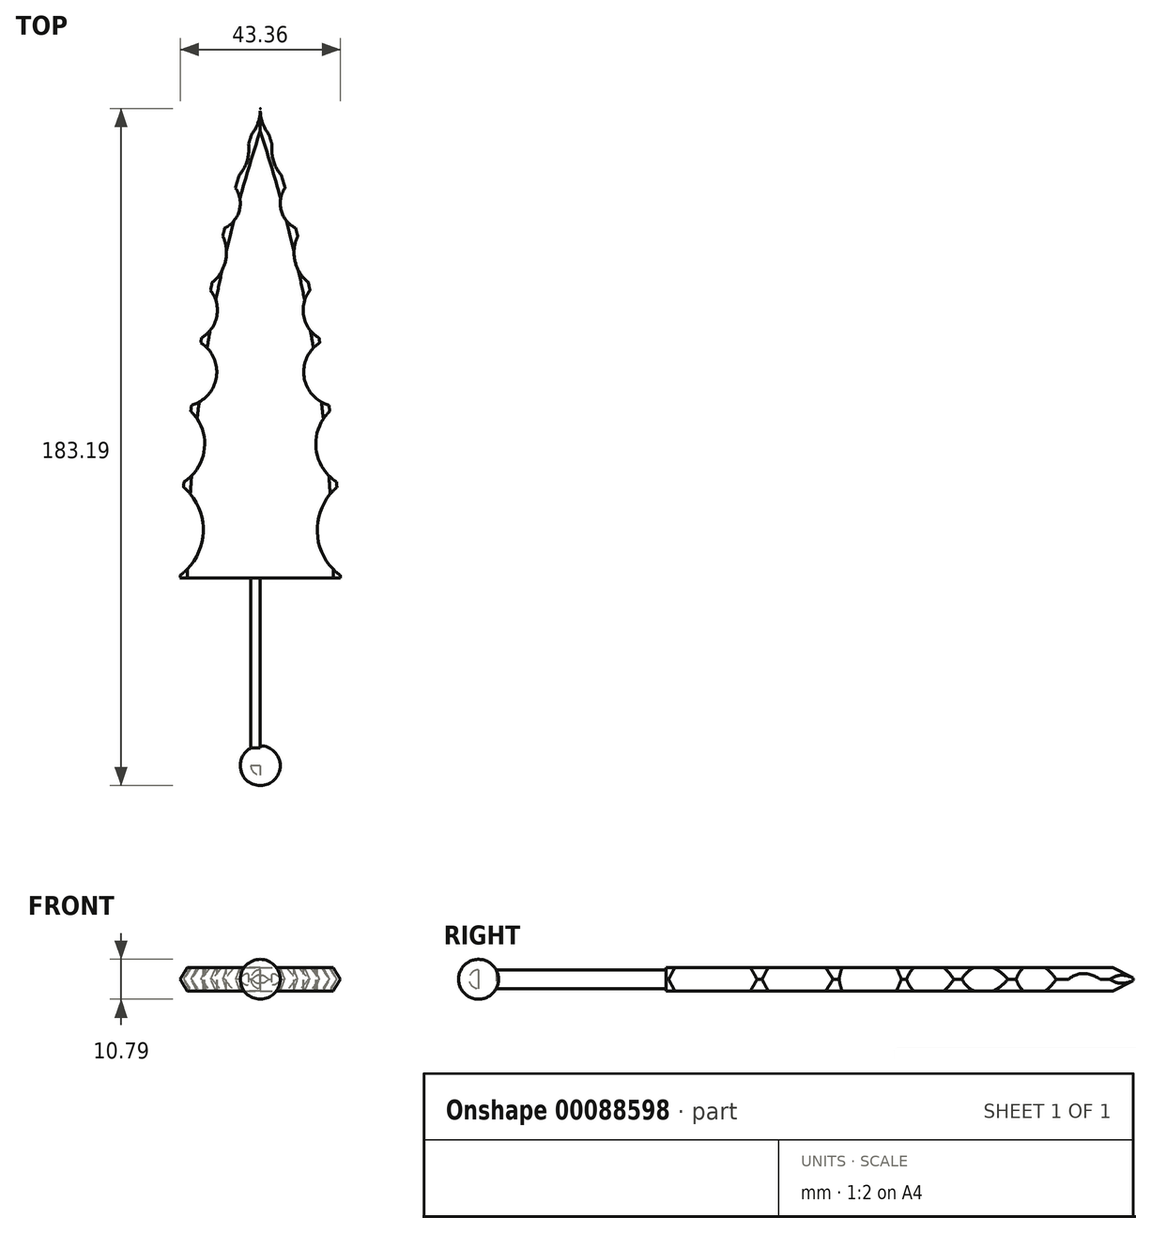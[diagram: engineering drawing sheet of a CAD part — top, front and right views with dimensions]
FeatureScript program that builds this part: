
annotation { "Feature Type Name" : "Feature", "Feature Type Description" : "" }
export const myFeature = defineFeature(function(context is Context, id is Id, definition is map)
    precondition{}
    {
        {
            var Q0;
            Q0=qCreatedBy(makeId("Top.planeOp"),FACE);
            var sketch = newSketch(context, id + "F0", { "sketchPlane" : qUnion([Q0])});
            skLineSegment(sketch, "E0", {"start": v(0, 0) * mm, "end": v(0, -127) * mm});
            skArc(sketch, "E1", {"start": v(0, 0) * mm, "mid": v(-15.98, -62.62) * mm, "end": v(-21.68, -127) * mm});
            skLineSegment(sketch, "E2", {"start": v(-21.68, -127) * mm, "end": v(0, -127) * mm});
            skSolve(sketch);
        }
        {
            var Q0;
            Q0=makeQuery(id+"F0.imprint","IMPRINT",FACE,{"disambiguationData":[TD([[makeQuery(id+"F0.imprint","IMPRINT",EDGE,{"derivedFrom":sQuery(id+"F0.wireOp",EDGE,"E0")}),-1.0]])]});
            extrude(context, id + "F1", {"entities" : qUnion([Q0]), "depth" : 6.35 * mm});
        }
        {
            var Q0;
            Q0=makeQuery(id+"F1.opExtrude","SWEPT_FACE",FACE,{"disambiguationData":[OSD([sQuery(id+"F0.wireOp",EDGE,"E0")])]});
            var sketch = newSketch(context, id + "F2", { "sketchPlane" : qUnion([Q0])});
            skLineSegment(sketch, "E3", {"start": v(0, 3.17) * mm, "end": v(-6.1, 6.35) * mm});
            skLineSegment(sketch, "E4", {"start": v(0, 3.18) * mm, "end": v(-6.1, 0) * mm});
            skLineSegment(sketch, "E5", {"start": v(-6.1, 6.35) * mm, "end": v(0, 6.35) * mm});
            skLineSegment(sketch, "E6", {"start": v(0, 6.35) * mm, "end": v(0, 0) * mm});
            skLineSegment(sketch, "E7", {"start": v(0, 0) * mm, "end": v(-6.1, 0) * mm});
            skSolve(sketch);
        }
        {
            var Q0;
            {var subQ0=sQuery(id+"F2.wireOp",EDGE,"E3");Q0=makeQuery(id+"F2.imprint","IMPRINT",FACE,{"disambiguationData":[TD([[makeQuery(id+"F2.imprint","IMPRINT",EDGE,{"derivedFrom":subQ0}),-1.0]])]});}
            var Q1;
            {var subQ0=sQuery(id+"F2.wireOp",EDGE,"E4");Q1=makeQuery(id+"F2.imprint","IMPRINT",FACE,{"disambiguationData":[TD([[makeQuery(id+"F2.imprint","IMPRINT",EDGE,{"derivedFrom":subQ0}),1.0]])]});}
            var Q2;
            Q2=makeQuery(id+"F1.opExtrude","CAP_EDGE",EDGE,{"disambiguationData":[OSD([sQuery(id+"F0.wireOp",EDGE,"E1")])],"isStart":false});
            sweep(context, id + "F3", {"operationType" : NewBodyOperationType.REMOVE, "profiles" : qUnion([Q0, Q1]), "path" : qUnion([Q2])});
        }
        {
            var Q0;
            Q0=makeQuery(id+"F1.opExtrude","CAP_FACE",FACE,{"disambiguationData":[OSD([sQuery(id+"F0.wireOp",EDGE,"E0"),sQuery(id+"F0.wireOp",EDGE,"E1"),sQuery(id+"F0.wireOp",EDGE,"E2")])],"isStart":false});
            var sketch = newSketch(context, id + "F4", { "sketchPlane" : qUnion([Q0])});
            skArc(sketch, "E8", {"start": v(-22.72, -127) * mm, "mid": v(-15.43, -114.58) * mm, "end": v(-21.75, -101.65) * mm});
            skPoint(sketch, "E8.startSnap0", {"position": v(-9.87, -127) * mm});
            skArc(sketch, "E9", {"start": v(-21.75, -101.65) * mm, "mid": v(-15.06, -91.49) * mm, "end": v(-20.44, -80.57) * mm});
            skArc(sketch, "E10", {"start": v(-20.44, -80.57) * mm, "mid": v(-11.9, -72.83) * mm, "end": v(-17.4, -62.7) * mm});
            skArc(sketch, "E11", {"start": v(-17.4, -62.7) * mm, "mid": v(-11.75, -56.2) * mm, "end": v(-14.55, -48.07) * mm});
            skPoint(sketch, "E11.endSnap0", {"position": v(-14.55, -65.78) * mm});
            skArc(sketch, "E12", {"start": v(-14.55, -48.07) * mm, "mid": v(-9.4, -41.24) * mm, "end": v(-11.12, -32.87) * mm});
            skArc(sketch, "E13", {"start": v(-11.12, -32.87) * mm, "mid": v(-5.63, -27.43) * mm, "end": v(-7.98, -20.08) * mm});
            skLineSegment(sketch, "E14", {"start": v(-22.72, -127) * mm, "end": v(-51.18, -45.67) * mm});
            skArc(sketch, "E15", {"start": v(-7.98, -20.08) * mm, "mid": v(-3.8, -14.83) * mm, "end": v(-3.43, -8.13) * mm});
            skArc(sketch, "E16", {"start": v(-3.43, -8.13) * mm, "mid": v(-0.15, -2.18) * mm, "end": v(-1.22, 4.54) * mm});
            skLineSegment(sketch, "E17", {"start": v(-1.22, 4.54) * mm, "end": v(-1.22, 22.29) * mm});
            skLineSegment(sketch, "E18", {"start": v(-51.18, -45.67) * mm, "end": v(-1.22, 22.29) * mm});
            skSolve(sketch);
        }
        {
            var Q0;
            Q0 = qSketchRegion(id + "F4", true);
            extrude(context, id + "F5", {"entities" : qUnion([Q0]), "operationType" : NewBodyOperationType.REMOVE, "oppositeDirection" : true, "depth" : 25.4 * mm});
        }
        {
            var Q0;
            Q0=makeQuery(id+"F5.boolean.opBoolean","SPLIT",BODY,{"disambiguationData":[OD(1.0)],"derivedFrom":makeQuery(id+"F1.opExtrude","SWEPT_BODY",BODY,{"disambiguationData":[OSD([sQuery(id+"F0.wireOp",EDGE,"E0"),sQuery(id+"F0.wireOp",EDGE,"E1"),sQuery(id+"F0.wireOp",EDGE,"E2")])]})});
            var Q1;
            {var subQ0=sQuery(id+"F0.wireOp",EDGE,"E1");var subQ1=sQuery(id+"F0.wireOp",EDGE,"E2");var subQ2=sQuery(id+"F0.wireOp",EDGE,"E0");Q1=makeQuery(id+"F5.boolean.opBoolean","SPLIT",FACE,{"disambiguationData":[TD([makeQuery(id+"F1.opExtrude","CAP_FACE",FACE,{"disambiguationData":[OSD([subQ2,subQ0,subQ1])],"isStart":true}),makeQuery(id+"F1.opExtrude","CAP_FACE",FACE,{"disambiguationData":[OSD([subQ2,subQ0,subQ1])],"isStart":false}),makeQuery(id+"F1.opExtrude","SWEPT_FACE",FACE,{"disambiguationData":[OSD([subQ1])]}),makeQuery(id+"F3.boolean.opBoolean","COPY",FACE,{"derivedFrom":makeQuery(id+"F3.opSweep","SWEPT_FACE",FACE,{"disambiguationData":[OSD([subQ0,sQuery(id+"F2.wireOp",EDGE,"E3")])]})}),makeQuery(id+"F3.boolean.opBoolean","COPY",FACE,{"derivedFrom":makeQuery(id+"F3.opSweep","SWEPT_FACE",FACE,{"disambiguationData":[OSD([subQ0,sQuery(id+"F2.wireOp",EDGE,"E4")])]})}),makeQuery(id+"F5.opExtrude","SWEPT_FACE",FACE,{"disambiguationData":[OSD([sQuery(id+"F4.wireOp",EDGE,"E16")])]})])],"derivedFrom":makeQuery(id+"F1.opExtrude","SWEPT_FACE",FACE,{"disambiguationData":[OSD([subQ2])]})});}
            mirror(context, id + "F6", {"operationType" : NewBodyOperationType.ADD, "entities" : qUnion([Q0]), "mirrorPlane" : qUnion([Q1])});
        }
        {
            var Q0;
            {var subQ0=makeQuery(id+"F1.opExtrude","SWEPT_FACE",FACE,{"disambiguationData":[OSD([sQuery(id+"F0.wireOp",EDGE,"E2")])]});Q0=makeQuery(id+"F6.boolean.opBoolean","MERGE",FACE,{"derivedFrom":[subQ0,makeQuery(id+"F6.opPattern","COPY",FACE,{"derivedFrom":subQ0,"instanceName":"1"})]});}
            var sketch = newSketch(context, id + "F7", { "sketchPlane" : qUnion([Q0])});
            skLineSegment(sketch, "E19.bottom", {"start": v(-19.75, 6.35) * mm, "end": v(19.75, 6.35) * mm});
            skLineSegment(sketch, "E19.top", {"start": v(-19.75, 0) * mm, "end": v(19.75, 0) * mm});
            skLineSegment(sketch, "E19.left", {"start": v(-19.75, 6.35) * mm, "end": v(-19.75, 0) * mm});
            skLineSegment(sketch, "E19.right", {"start": v(19.75, 6.35) * mm, "end": v(19.75, 0) * mm});
            skLineSegment(sketch, "E20", {"start": v(-19.75, 6.35) * mm, "end": v(-6.58, 6.35) * mm});
            skLineSegment(sketch, "E21", {"start": v(19.75, 6.35) * mm, "end": v(6.58, 6.35) * mm});
            skLineSegment(sketch, "E22", {"start": v(-6.58, 6.35) * mm, "end": v(6.58, 6.35) * mm});
            skLineSegment(sketch, "E23", {"start": v(-6.58, 6.35) * mm, "end": v(-6.58, 0) * mm});
            skLineSegment(sketch, "E24", {"start": v(6.58, 6.35) * mm, "end": v(6.58, 0) * mm});
            skLineSegment(sketch, "E25", {"start": v(-6.58, 3.18) * mm, "end": v(6.58, 3.18) * mm});
            skCircle(sketch, "E26", {"center": v(0, 3.18) * mm, "radius": 2.54 * mm});
            skSolve(sketch);
        }
        {
            var Q0;
            {var subQ0=sQuery(id+"F7.wireOp",EDGE,"TZ6vj6Sh-qNe0-tSPx-zquS-x5aDAgaGdUHA");var subQ1=sQuery(id+"F7.wireOp",EDGE,"E25");var subQ2=makeQuery(id+"F7.imprint","INTERSECT",VERTEX,{"disambiguationData":[OD(0.0)],"derivedFrom":[subQ1,subQ0]});Q0=makeQuery(id+"F7.imprint","IMPRINT",FACE,{"disambiguationData":[TD([[makeQuery(id+"F7.imprint","IMPRINT",EDGE,{"disambiguationData":[TD([[subQ2,-1.0]])],"derivedFrom":subQ1}),1.0]])]});}
            var Q1;
            {var subQ0=sQuery(id+"F7.wireOp",EDGE,"TZ6vj6Sh-qNe0-tSPx-zquS-x5aDAgaGdUHA");var subQ1=sQuery(id+"F7.wireOp",EDGE,"E25");var subQ2=makeQuery(id+"F7.imprint","INTERSECT",VERTEX,{"disambiguationData":[OD(0.0)],"derivedFrom":[subQ1,subQ0]});Q1=makeQuery(id+"F7.imprint","IMPRINT",FACE,{"disambiguationData":[TD([[makeQuery(id+"F7.imprint","IMPRINT",EDGE,{"disambiguationData":[TD([[subQ2,-1.0]])],"derivedFrom":subQ1}),-1.0]])]});}
            extrude(context, id + "F8", {"entities" : qUnion([Q0, Q1]), "operationType" : NewBodyOperationType.ADD, "depth" : 50.8 * mm});
        }
        {
            var Q0;
            Q0=makeQuery(id+"F8.opExtrude","CAP_FACE",FACE,{"disambiguationData":[OSD([sQuery(id+"F7.wireOp",EDGE,"E26")])],"isStart":false});
            var sketch = newSketch(context, id + "F9", { "sketchPlane" : qUnion([Q0])});
            skCircle(sketch, "E27", {"center": v(0, 3.18) * mm, "radius": 5.4 * mm});
            skLineSegment(sketch, "E28", {"start": v(-5.4, 3.18) * mm, "end": v(5.4, 3.18) * mm});
            skSolve(sketch);
        }
        {
            var Q0;
            {var subQ0=sQuery(id+"F9.wireOp",EDGE,"E28");var subQ1=sQuery(id+"F9.wireOp",EDGE,"E27");var subQ2=makeQuery(id+"F9.imprint","INTERSECT",VERTEX,{"disambiguationData":[OD(0.0)],"derivedFrom":[subQ1,subQ0]});Q0=makeQuery(id+"F9.imprint","IMPRINT",FACE,{"disambiguationData":[TD([[makeQuery(id+"F9.imprint","IMPRINT",EDGE,{"disambiguationData":[TD([[subQ2,1.0]])],"derivedFrom":subQ1}),1.0]])]});}
            var Q1;
            Q1=sQuery(id+"F9.wireOp",EDGE,"E28");
            revolve(context, id + "F10", {"operationType" : NewBodyOperationType.ADD, "entities" : qUnion([Q0]), "axis" : qUnion([Q1]), "revolveType" : RevolveType.FULL});
        }
    });
